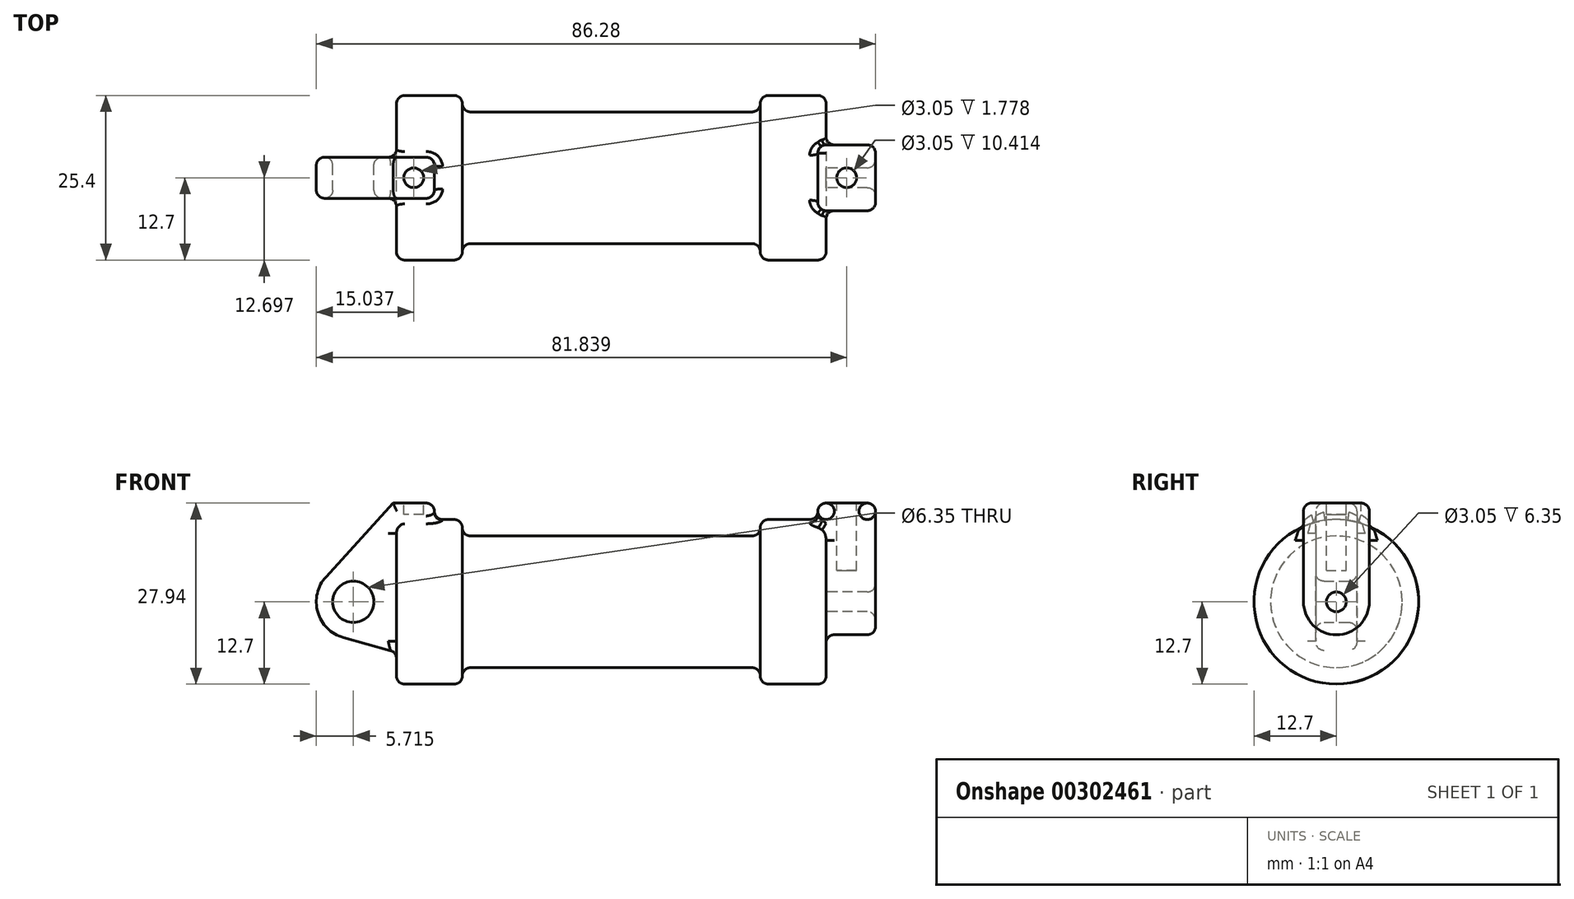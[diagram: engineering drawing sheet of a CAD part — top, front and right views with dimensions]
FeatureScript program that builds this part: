
annotation { "Feature Type Name" : "Feature", "Feature Type Description" : "" }
export const myFeature = defineFeature(function(context is Context, id is Id, definition is map)
    precondition{}
    {
        {
            var Q0;
            Q0=qCreatedBy(makeId("Front.planeOp"),FACE);
            var sketch = newSketch(context, id + "F0", { "sketchPlane" : qUnion([Q0])});
            skLineSegment(sketch, "E0", {"start": v(0, 0) * mm, "end": v(0, 12.7) * mm});
            skLineSegment(sketch, "E1", {"start": v(0, 12.7) * mm, "end": v(10.16, 12.7) * mm});
            skLineSegment(sketch, "E2", {"start": v(10.16, 12.7) * mm, "end": v(10.16, 10.16) * mm});
            skLineSegment(sketch, "E3", {"start": v(10.16, 10.16) * mm, "end": v(56.13, 10.16) * mm});
            skLineSegment(sketch, "E4", {"start": v(56.13, 10.16) * mm, "end": v(56.13, 12.7) * mm});
            skLineSegment(sketch, "E5", {"start": v(56.13, 12.7) * mm, "end": v(66.3, 12.7) * mm});
            skLineSegment(sketch, "E6", {"start": v(66.3, 12.7) * mm, "end": v(66.3, 0) * mm});
            skLineSegment(sketch, "E7", {"start": v(66.3, 0) * mm, "end": v(0, 0) * mm});
            skLineSegment(sketch, "E8", {"start": v(5.84, 15.24) * mm, "end": v(-0.5, 15.24) * mm});
            skLineSegment(sketch, "E9", {"start": v(-0.5, 15.24) * mm, "end": v(-10.88, 3.85) * mm});
            skLineSegment(sketch, "E10", {"start": v(0, 0) * mm, "end": v(-6.65, 0) * mm});
            skCircle(sketch, "E11", {"center": v(-6.65, 0) * mm, "radius": 5.72 * mm});
            skCircle(sketch, "E12", {"center": v(-6.65, 0) * mm, "radius": 3.18 * mm});
            skLineSegment(sketch, "E13", {"start": v(5.84, 15.24) * mm, "end": v(5.84, -9.4) * mm});
            skLineSegment(sketch, "E14", {"start": v(5.84, -9.4) * mm, "end": v(-8.18, -5.5) * mm});
            skSolve(sketch);
        }
        {
            var Q0;
            {var subQ0=sQuery(id+"F0.wireOp",EDGE,"E2");Q0=makeQuery(id+"F0.imprint","IMPRINT",FACE,{"disambiguationData":[TD([[makeQuery(id+"F0.imprint","IMPRINT",EDGE,{"derivedFrom":subQ0}),-1.0]])]});}
            var Q1;
            {var subQ0=sQuery(id+"F0.wireOp",EDGE,"E0");Q1=makeQuery(id+"F0.imprint","IMPRINT",FACE,{"disambiguationData":[TD([[makeQuery(id+"F0.imprint","IMPRINT",EDGE,{"derivedFrom":subQ0}),-1.0]])]});}
            var Q2;
            Q2=sQuery(id+"F0.wireOp",EDGE,"E7");
            revolve(context, id + "F1", {"entities" : qUnion([Q0, Q1]), "axis" : qUnion([Q2]), "revolveType" : RevolveType.FULL});
        }
        {
            var Q0;
            {var subQ1=sQuery(id+"F0.wireOp",EDGE,"E0");Q0=makeQuery(id+"F0.imprint","IMPRINT",FACE,{"disambiguationData":[TD([[makeQuery(id+"F0.imprint","IMPRINT",EDGE,{"derivedFrom":subQ1}),1.0]])]});}
            var Q1;
            {var subQ0=sQuery(id+"F0.wireOp",EDGE,"E14");Q1=makeQuery(id+"F0.imprint","IMPRINT",FACE,{"disambiguationData":[TD([[makeQuery(id+"F0.imprint","IMPRINT",EDGE,{"derivedFrom":subQ0}),-1.0]])]});}
            var Q2;
            {var subQ5=sQuery(id+"F0.wireOp",EDGE,"E12");Q2=makeQuery(id+"F0.imprint","IMPRINT",FACE,{"disambiguationData":[TD([[makeQuery(id+"F0.imprint","IMPRINT",EDGE,{"derivedFrom":subQ5}),-1.0]])]});}
            var Q3;
            {var subQ0=sQuery(id+"F0.wireOp",EDGE,"E0");Q3=makeQuery(id+"F0.imprint","IMPRINT",FACE,{"disambiguationData":[TD([[makeQuery(id+"F0.imprint","IMPRINT",EDGE,{"derivedFrom":subQ0}),-1.0]])]});}
            extrude(context, id + "F2", {"entities" : qUnion([Q0, Q1, Q2, Q3]), "operationType" : NewBodyOperationType.ADD, "endBound" : BoundingType.SYMMETRIC, "depth" : 6.35 * mm});
        }
        {
            var Q0;
            Q0=makeQuery(id+"F1.opRevolve","SWEPT_FACE",FACE,{"disambiguationData":[OSD([sQuery(id+"F0.wireOp",EDGE,"E6")])]});
            var sketch = newSketch(context, id + "F3", { "sketchPlane" : qUnion([Q0])});
            skCircle(sketch, "E15", {"center": v(0, 0) * mm, "radius": 1.52 * mm});
            skCircle(sketch, "E16", {"center": v(0, 0) * mm, "radius": 5.08 * mm});
            skLineSegment(sketch, "E17", {"start": v(-5.08, 0) * mm, "end": v(-5.08, 15.24) * mm});
            skLineSegment(sketch, "E18", {"start": v(5.08, 0) * mm, "end": v(5.08, 15.24) * mm});
            skLineSegment(sketch, "E19", {"start": v(5.08, 15.24) * mm, "end": v(-5.08, 15.24) * mm});
            skSolve(sketch);
        }
        {
            var Q0;
            {var subQ0=sQuery(id+"F3.wireOp",EDGE,"E19");Q0=makeQuery(id+"F3.imprint","IMPRINT",FACE,{"disambiguationData":[TD([[makeQuery(id+"F3.imprint","IMPRINT",EDGE,{"derivedFrom":subQ0}),1.0]])]});}
            var Q1;
            {var subQ0=sQuery(id+"F3.wireOp",EDGE,"E17");var subQ1=sQuery(id+"F3.wireOp",EDGE,"E16");var subQ2=makeQuery(id+"F3.imprint","INTERSECT",VERTEX,{"derivedFrom":[subQ1,subQ0]});Q1=makeQuery(id+"F3.imprint","IMPRINT",FACE,{"disambiguationData":[TD([[makeQuery(id+"F3.imprint","IMPRINT",EDGE,{"disambiguationData":[TD([[subQ2,1.0]])],"derivedFrom":subQ1}),-1.0]])]});}
            var Q2;
            Q2=makeQuery(id+"F3.imprint","IMPRINT",FACE,{"disambiguationData":[TD([[makeQuery(id+"F3.imprint","IMPRINT",EDGE,{"derivedFrom":sQuery(id+"F3.wireOp",EDGE,"E15")}),-1.0]])]});
            extrude(context, id + "F4", {"entities" : qUnion([Q0, Q1, Q2]), "operationType" : NewBodyOperationType.ADD, "depth" : 7.62 * mm, "hasSecondDirection" : true, "secondDirectionOppositeDirection" : true, "secondDirectionDepth" : 1.27 * mm});
        }
        {
            var Q0;
            Q0=makeQuery(id+"F2.opExtrude","SWEPT_FACE",FACE,{"disambiguationData":[OSD([sQuery(id+"F0.wireOp",EDGE,"E8")])]});
            var sketch = newSketch(context, id + "F5", { "sketchPlane" : qUnion([Q0])});
            skCircle(sketch, "E20", {"center": v(2.67, 0) * mm, "radius": 1.52 * mm});
            skPoint(sketch, "E20.centerSnap0", {"position": v(2.67, 3.18) * mm});
            skPoint(sketch, "E20.centerSnap1", {"position": v(5.84, 0) * mm});
            skSolve(sketch);
        }
        {
            var Q0;
            Q0=makeQuery(id+"F5.imprint","IMPRINT",FACE,{"disambiguationData":[TD([[makeQuery(id+"F5.imprint","IMPRINT",EDGE,{"derivedFrom":sQuery(id+"F5.wireOp",EDGE,"E20")}),1.0]])]});
            extrude(context, id + "F6", {"entities" : qUnion([Q0]), "operationType" : NewBodyOperationType.REMOVE, "oppositeDirection" : true, "depth" : 1.78 * mm});
        }
        {
            var Q0;
            Q0=makeQuery(id+"F4.opExtrude","SWEPT_FACE",FACE,{"disambiguationData":[OSD([sQuery(id+"F3.wireOp",EDGE,"E19")])]});
            var sketch = newSketch(context, id + "F7", { "sketchPlane" : qUnion([Q0])});
            skCircle(sketch, "E21", {"center": v(69.47, 0) * mm, "radius": 1.52 * mm});
            skPoint(sketch, "E21.centerSnap0", {"position": v(69.47, 5.07) * mm});
            skPoint(sketch, "E21.centerSnap1", {"position": v(73.91, 0) * mm});
            skSolve(sketch);
        }
        {
            var Q0;
            Q0 = qSketchRegion(id + "F7", true);
            extrude(context, id + "F8", {"entities" : qUnion([Q0]), "operationType" : NewBodyOperationType.REMOVE, "oppositeDirection" : true, "depth" : 10.4 * mm});
        }
        {
            var Q0;
            Q0=makeQuery(id+"F1.opRevolve","SWEPT_EDGE",EDGE,{"disambiguationData":[OSD([sQuery(id+"F0.wireOp",EDGE,"E0"),sQuery(id+"F0.wireOp",EDGE,"E1")])]});
            var Q1;
            Q1=makeQuery(id+"F1.opRevolve","SWEPT_EDGE",EDGE,{"disambiguationData":[OSD([sQuery(id+"F0.wireOp",EDGE,"E1"),sQuery(id+"F0.wireOp",EDGE,"E2")])]});
            var Q2;
            Q2=makeQuery(id+"F1.opRevolve","SWEPT_EDGE",EDGE,{"disambiguationData":[OSD([sQuery(id+"F0.wireOp",EDGE,"E4"),sQuery(id+"F0.wireOp",EDGE,"E5")])]});
            var Q3;
            Q3=makeQuery(id+"F1.opRevolve","SWEPT_EDGE",EDGE,{"disambiguationData":[OSD([sQuery(id+"F0.wireOp",EDGE,"E5"),sQuery(id+"F0.wireOp",EDGE,"E6")])]});
            fillet(context, id + "F9", {"entities" : qUnion([Q0, Q1, Q2, Q3]), "radius" : 1.27 * mm, "tangentPropagation" : true, "allowEdgeOverflow" : false});
        }
        {
            var Q0;
            Q0=makeQuery(id+"F1.opRevolve","SWEPT_FACE",FACE,{"disambiguationData":[OSD([sQuery(id+"F0.wireOp",EDGE,"E3")])]});
            fillet(context, id + "F10", {"entities" : qUnion([Q0]), "radius" : 1.27 * mm, "tangentPropagation" : true, "allowEdgeOverflow" : false});
        }
        {
            var Q0;
            Q0=makeQuery(id+"F2.opExtrude","CAP_EDGE",EDGE,{"disambiguationData":[OSD([sQuery(id+"F0.wireOp",EDGE,"E9")])],"isStart":false});
            var Q1;
            Q1=makeQuery(id+"F2.opExtrude","CAP_EDGE",EDGE,{"disambiguationData":[OSD([sQuery(id+"F0.wireOp",EDGE,"E8")])],"isStart":false});
            var Q2;
            Q2=makeQuery(id+"F2.opExtrude","CAP_EDGE",EDGE,{"disambiguationData":[OSD([sQuery(id+"F0.wireOp",EDGE,"E9")])],"isStart":true});
            var Q3;
            Q3=makeQuery(id+"F2.opExtrude","CAP_EDGE",EDGE,{"disambiguationData":[OSD([sQuery(id+"F0.wireOp",EDGE,"E8")])],"isStart":true});
            var Q4;
            Q4=makeQuery(id+"F2.opExtrude","SWEPT_EDGE",EDGE,{"disambiguationData":[OSD([sQuery(id+"F0.wireOp",EDGE,"E8"),sQuery(id+"F0.wireOp",EDGE,"E13")])]});
            var Q5;
            Q5=makeQuery(id+"F2.opExtrude","CAP_EDGE",EDGE,{"disambiguationData":[OSD([sQuery(id+"F0.wireOp",EDGE,"E11")])],"isStart":true});
            var Q6;
            Q6=makeQuery(id+"F2.opExtrude","CAP_EDGE",EDGE,{"disambiguationData":[OSD([sQuery(id+"F0.wireOp",EDGE,"E14")])],"isStart":true});
            var Q7;
            Q7=makeQuery(id+"F2.opExtrude","CAP_EDGE",EDGE,{"disambiguationData":[OSD([sQuery(id+"F0.wireOp",EDGE,"E14")])],"isStart":false});
            var Q8;
            Q8=makeQuery(id+"F2.opExtrude","CAP_EDGE",EDGE,{"disambiguationData":[OSD([sQuery(id+"F0.wireOp",EDGE,"E11")])],"isStart":false});
            fillet(context, id + "F11", {"entities" : qUnion([Q0, Q1, Q2, Q3, Q4, Q5, Q6, Q7, Q8]), "radius" : 1.27 * mm, "tangentPropagation" : true, "allowEdgeOverflow" : false});
        }
        {
            var Q0;
            Q0=makeQuery(id+"F1.opRevolve","SWEPT_FACE",FACE,{"disambiguationData":[OSD([sQuery(id+"F0.wireOp",EDGE,"E1")])]});
            var Q1;
            Q1=makeQuery(id+"F2.opExtrude","CAP_FACE",FACE,{"disambiguationData":[OSD([sQuery(id+"F0.wireOp",EDGE,"E8"),sQuery(id+"F0.wireOp",EDGE,"E9"),sQuery(id+"F0.wireOp",EDGE,"E11"),sQuery(id+"F0.wireOp",EDGE,"E12"),sQuery(id+"F0.wireOp",EDGE,"E13"),sQuery(id+"F0.wireOp",EDGE,"E14")])],"isStart":false});
            var Q2;
            Q2=makeQuery(id+"F2.opExtrude","CAP_FACE",FACE,{"disambiguationData":[OSD([sQuery(id+"F0.wireOp",EDGE,"E8"),sQuery(id+"F0.wireOp",EDGE,"E9"),sQuery(id+"F0.wireOp",EDGE,"E11"),sQuery(id+"F0.wireOp",EDGE,"E12"),sQuery(id+"F0.wireOp",EDGE,"E13"),sQuery(id+"F0.wireOp",EDGE,"E14")])],"isStart":true});
            var Q3;
            Q3=makeQuery(id+"F2.opExtrude","SWEPT_FACE",FACE,{"disambiguationData":[OSD([sQuery(id+"F0.wireOp",EDGE,"E13")])]});
            fillet(context, id + "F12", {"entities" : qUnion([Q0, Q1, Q2, Q3]), "radius" : 1.27 * mm, "tangentPropagation" : true, "allowEdgeOverflow" : false});
        }
        {
            var Q0;
            Q0=makeQuery(id+"F4.opExtrude","SWEPT_FACE",FACE,{"disambiguationData":[OSD([sQuery(id+"F3.wireOp",EDGE,"E17")])]});
            var Q1;
            Q1=makeQuery(id+"F4.opExtrude","SWEPT_FACE",FACE,{"disambiguationData":[OSD([sQuery(id+"F3.wireOp",EDGE,"E18")])]});
            var Q2;
            Q2=makeQuery(id+"F4.opExtrude","SWEPT_FACE",FACE,{"disambiguationData":[OSD([sQuery(id+"F3.wireOp",EDGE,"E16")])]});
            var Q3;
            Q3=makeQuery(id+"F4.boolean.opBoolean","SPLIT",FACE,{"disambiguationData":[TD([makeQuery(id+"F1.opRevolve","SWEPT_FACE",FACE,{"disambiguationData":[OSD([sQuery(id+"F0.wireOp",EDGE,"E5")])]})])],"derivedFrom":makeQuery(id+"F1.opRevolve","SWEPT_FACE",FACE,{"disambiguationData":[OSD([sQuery(id+"F0.wireOp",EDGE,"E6")])]})});
            var Q4;
            Q4=makeQuery(id+"F4.opExtrude","CAP_FACE",FACE,{"disambiguationData":[OSD([sQuery(id+"F3.wireOp",EDGE,"E15"),sQuery(id+"F3.wireOp",EDGE,"E16"),sQuery(id+"F3.wireOp",EDGE,"E17"),sQuery(id+"F3.wireOp",EDGE,"E18"),sQuery(id+"F3.wireOp",EDGE,"E19")])],"isStart":false});
            var Q5;
            Q5=makeQuery(id+"F9.opFillet","BLEND_FACE",FACE,{"disambiguationData":[OSD([sQuery(id+"F0.wireOp",EDGE,"E5"),sQuery(id+"F0.wireOp",EDGE,"E6")])]});
            var Q6;
            Q6=makeQuery(id+"F4.opExtrude","CAP_FACE",FACE,{"disambiguationData":[OSD([sQuery(id+"F3.wireOp",EDGE,"E15"),sQuery(id+"F3.wireOp",EDGE,"E16"),sQuery(id+"F3.wireOp",EDGE,"E17"),sQuery(id+"F3.wireOp",EDGE,"E18"),sQuery(id+"F3.wireOp",EDGE,"E19")])],"isStart":true});
            fillet(context, id + "F13", {"entities" : qUnion([Q0, Q1, Q2, Q3, Q4, Q5, Q6]), "radius" : 1.27 * mm, "tangentPropagation" : true, "allowEdgeOverflow" : false});
        }
    });
